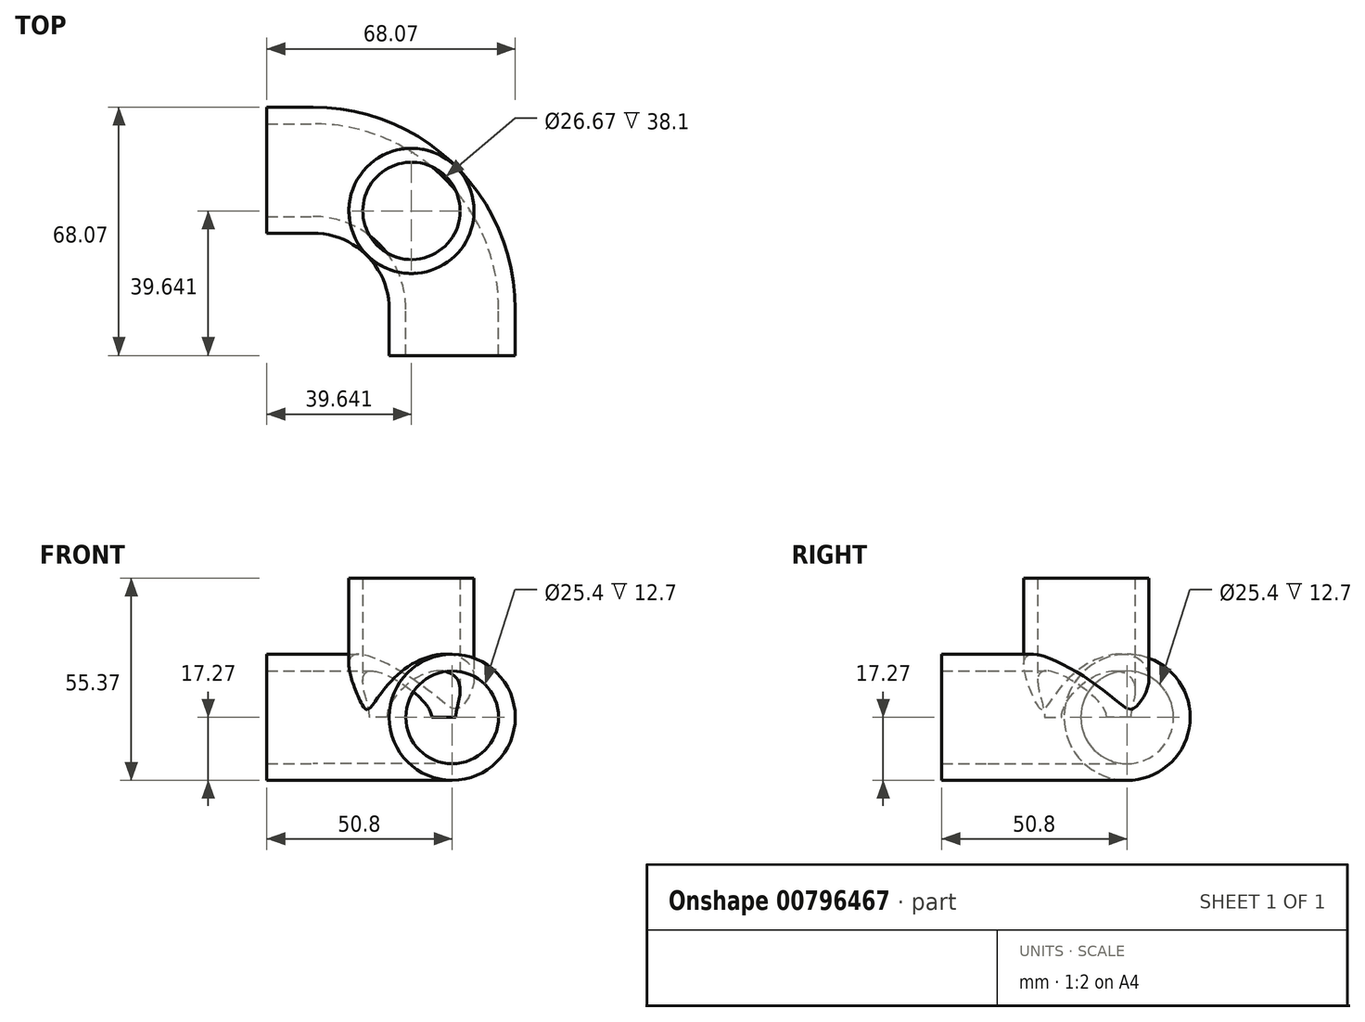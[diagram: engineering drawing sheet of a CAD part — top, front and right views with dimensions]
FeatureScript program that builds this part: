
annotation { "Feature Type Name" : "Feature", "Feature Type Description" : "" }
export const myFeature = defineFeature(function(context is Context, id is Id, definition is map)
    precondition{}
    {
        {
            var Q0;
            Q0=qCreatedBy(makeId("Right.planeOp"),FACE);
            var sketch = newSketch(context, id + "F0", { "sketchPlane" : qUnion([Q0])});
            skCircle(sketch, "E0", {"center": v(0, 0) * mm, "radius": 12.7 * mm});
            skCircle(sketch, "E1.0", {"center": v(0, 0) * mm, "radius": 17.27 * mm});
            skLineSegment(sketch, "E2", {"start": v(0, 0) * mm, "end": v(-38.1, 0) * mm});
            skLineSegment(sketch, "E3", {"start": v(-38.1, 0) * mm, "end": v(-38.1, 12.7) * mm});
            skSolve(sketch);
        }
        {
            var Q0;
            Q0=makeQuery(id+"F0.imprint","IMPRINT",FACE,{"disambiguationData":[TD([[makeQuery(id+"F0.imprint","IMPRINT",EDGE,{"derivedFrom":sQuery(id+"F0.wireOp",EDGE,"E0")}),-1.0]])]});
            var Q1;
            Q1=sQuery(id+"F0.wireOp",EDGE,"E3");
            revolve(context, id + "F1", {"surfaceOperationType" : NewSurfaceOperationType.NEW, "entities" : qUnion([Q0]), "axis" : qUnion([Q1]), "revolveType" : RevolveType.ONE_DIRECTION, "oppositeDirection" : true, "angle" : 90 * degree});
        }
        {
            var Q0;
            Q0=makeQuery(id+"F1.opRevolve","CAP_FACE",FACE,{"disambiguationData":[OSD([sQuery(id+"F0.wireOp",EDGE,"E0"),sQuery(id+"F0.wireOp",EDGE,"E1.0")])],"isStart":false});
            extrude(context, id + "F2", {"entities" : qUnion([Q0]), "operationType" : NewBodyOperationType.ADD, "depth" : 12.7 * mm, "offsetDistance" : 25.4 * mm});
        }
        {
            var Q0;
            Q0=makeQuery(id+"F1.opRevolve","CAP_FACE",FACE,{"disambiguationData":[OSD([sQuery(id+"F0.wireOp",EDGE,"E0"),sQuery(id+"F0.wireOp",EDGE,"E1.0")])],"isStart":true});
            extrude(context, id + "F3", {"entities" : qUnion([Q0]), "operationType" : NewBodyOperationType.ADD, "depth" : 12.7 * mm, "offsetDistance" : 25.4 * mm});
        }
        {
            var Q0;
            Q0=qCreatedBy(makeId("Top.planeOp"),FACE);
            var sketch = newSketch(context, id + "F4", { "sketchPlane" : qUnion([Q0])});
            skLineSegment(sketch, "E4", {"start": v(0, 0) * mm, "end": v(0, -38.1) * mm});
            skLineSegment(sketch, "E5", {"start": v(0, -38.1) * mm, "end": v(53.88, 15.78) * mm});
            skLineSegment(sketch, "E6", {"start": v(0, -38.1) * mm, "end": v(26.94, -11.16) * mm});
            skCircle(sketch, "E7", {"center": v(26.94, -11.16) * mm, "radius": 13.34 * mm});
            skCircle(sketch, "E8.0", {"center": v(26.94, -11.16) * mm, "radius": 17.14 * mm});
            skSolve(sketch);
        }
        {
            var Q0;
            Q0 = qSketchRegion(id + "F4", true);
            extrude(context, id + "F5", {"entities" : qUnion([Q0]), "operationType" : NewBodyOperationType.ADD, "depth" : 38.1 * mm, "offsetDistance" : 25.4 * mm});
        }
        {
            var Q0;
            Q0=qCreatedBy(makeId("Top.planeOp"),FACE);
            var sketch = newSketch(context, id + "F6", { "sketchPlane" : qUnion([Q0])});
            skCircle(sketch, "E9", {"center": v(26.94, -11.16) * mm, "radius": 13.34 * mm});
            skSolve(sketch);
        }
        {
            var Q0;
            Q0=sQuery(id+"F6.wireOp",VERTEX,"E9.center");
            var Q1;
            Q1=makeQuery(id+"F1.opRevolve","SWEPT_BODY",BODY,{"disambiguationData":[OSD([sQuery(id+"F0.wireOp",EDGE,"E0"),sQuery(id+"F0.wireOp",EDGE,"E1.0")])]});
            hole(context, id + "F7", {"style" : HoleStyle.SIMPLE, "endStyle" : HoleEndStyle.THROUGH, "oppositeDirection" : true, "holeDiameter" : 26.67 * mm, "majorDiameter" : 6.35 * mm, "isTappedThrough" : true, "tappedDepth" : 12.7 * mm, "tapClearance" : 3, "locations" : qUnion([Q0]), "scope" : qUnion([Q1])});
        }
        {
            var Q0;
            Q0=makeQuery(id+"F0.imprint","IMPRINT",FACE,{"disambiguationData":[TD([[makeQuery(id+"F0.imprint","IMPRINT",EDGE,{"derivedFrom":sQuery(id+"F0.wireOp",EDGE,"E0")}),1.0]])]});
            var Q1;
            Q1=sQuery(id+"F0.wireOp",EDGE,"E3");
            revolve(context, id + "F8", {"operationType" : NewBodyOperationType.REMOVE, "surfaceOperationType" : NewSurfaceOperationType.NEW, "entities" : qUnion([Q0]), "axis" : qUnion([Q1]), "revolveType" : RevolveType.ONE_DIRECTION, "oppositeDirection" : true, "angle" : 90 * degree});
        }
    });
